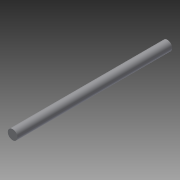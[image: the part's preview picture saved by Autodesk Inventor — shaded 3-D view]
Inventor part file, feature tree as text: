
AUTODESK INVENTOR PART (.ipt)
format: ipt  version: 2015 SP1 (Build 190203100, 203)  size: 88,064 bytes
history: native  units: in
note: dims shown in document units (in); Inventor stores cm internally (conversion verified against a paired STEP export)
features: extrude x2, sketch x2, projected_geometry x1
ambient origin geometry x8: Origin, YZ Plane, XZ Plane, XY Plane, X Axis, Y Axis, Z Axis, Center Point
bodies: Solid1 (feature_tree)
feature tree (5):
  extrude  "Extrusion1"  Depth=5.5in TaperAngle=0.0deg
  extrude  "Extrusion2"  TaperAngle=60.0deg  [1 undecoded]
  sketch  "Sketch1"  dims[d0=0.375in d1=5.5in d2=0.0in]
  sketch  "Sketch2"  dims[d3=0.2812in d4=60.0deg d5=2.3622in d7=360.0deg d9=0.1825in d10=0.0in]
  projected_geometry  "Projected Loop1"
note: 1 required parameter value undecoded (feature->parameter linkage not recoverable at this tier; creation-order binding heuristic only, values carry confidence <= 0.55)
